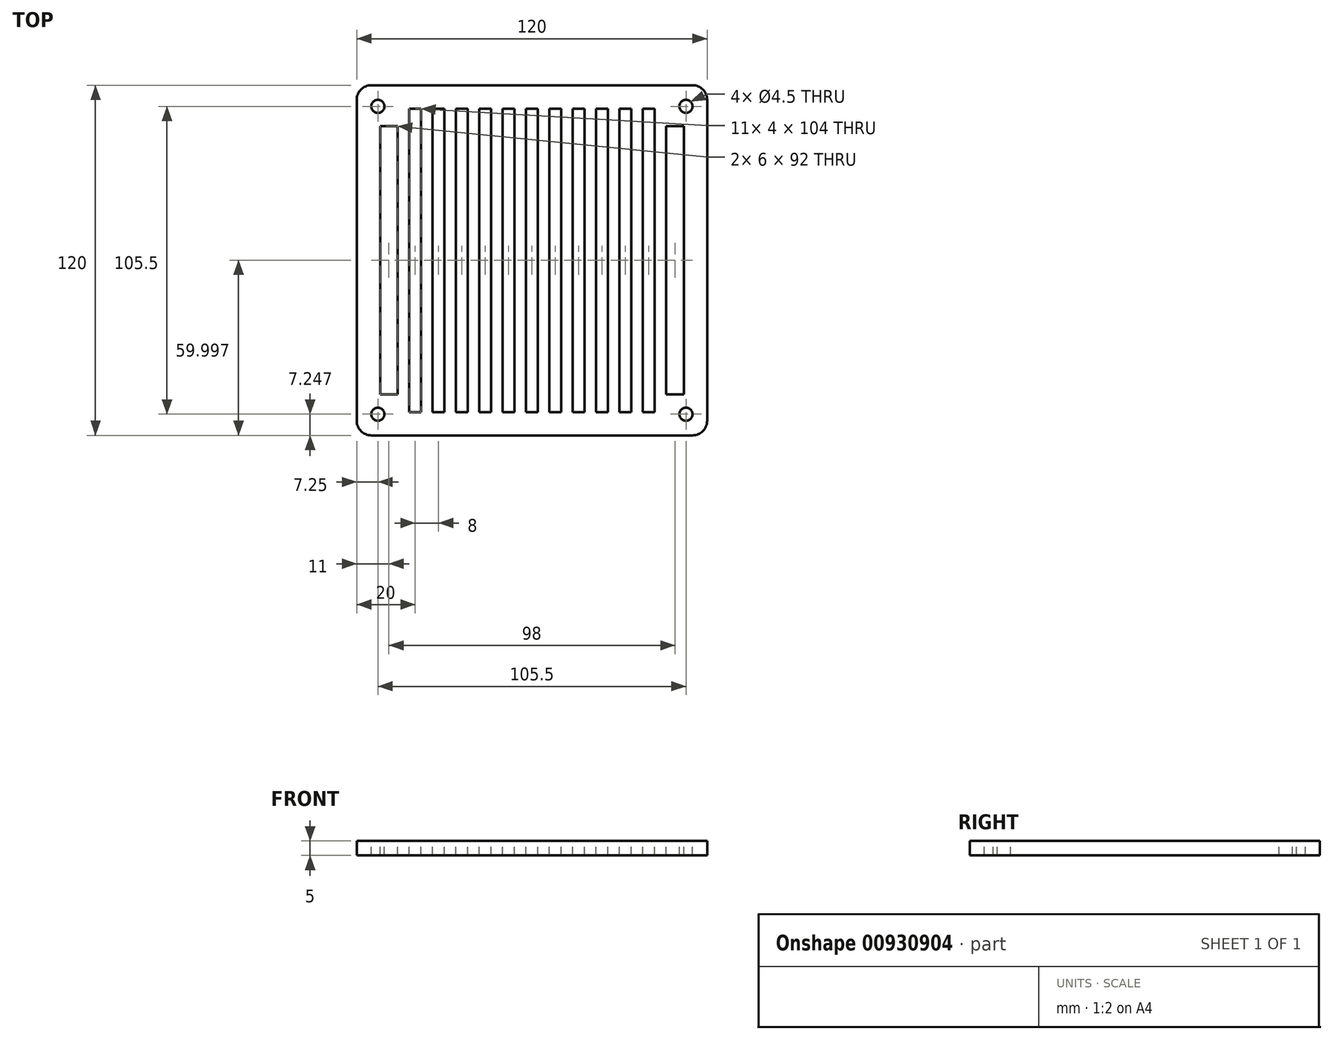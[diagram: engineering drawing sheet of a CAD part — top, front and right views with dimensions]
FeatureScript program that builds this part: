
annotation { "Feature Type Name" : "Feature", "Feature Type Description" : "" }
export const myFeature = defineFeature(function(context is Context, id is Id, definition is map)
    precondition{}
    {
        {
            var Q0;
            Q0=qCreatedBy(makeId("Top.planeOp"),FACE);
            var sketch = newSketch(context, id + "F0", { "sketchPlane" : qUnion([Q0])});
            skLineSegment(sketch, "E0", {"start": v(63.6, 60.5) * mm, "end": v(63.6, -59.5) * mm});
            skLineSegment(sketch, "E1", {"start": v(63.6, -59.5) * mm, "end": v(-56.4, -59.5) * mm});
            skLineSegment(sketch, "E2", {"start": v(63.6, 60.5) * mm, "end": v(-56.4, 60.5) * mm});
            skLineSegment(sketch, "E3", {"start": v(-56.4, 60.5) * mm, "end": v(-56.4, -59.5) * mm});
            skSolve(sketch);
        }
        {
            var Q0;
            Q0 = qSketchRegion(id + "F0", true);
            extrude(context, id + "F1", {"entities" : qUnion([Q0]), "depth" : 5 * mm, "offsetDistance" : 25 * mm});
        }
        {
            var Q0;
            Q0=makeQuery(id+"F1.opExtrude","SWEPT_EDGE",EDGE,{"disambiguationData":[OSD([sQuery(id+"F0.wireOp",EDGE,"E2"),sQuery(id+"F0.wireOp",EDGE,"E3")])]});
            var Q1;
            Q1=makeQuery(id+"F1.opExtrude","SWEPT_EDGE",EDGE,{"disambiguationData":[OSD([sQuery(id+"F0.wireOp",EDGE,"E0"),sQuery(id+"F0.wireOp",EDGE,"E2")])]});
            var Q2;
            Q2=makeQuery(id+"F1.opExtrude","SWEPT_EDGE",EDGE,{"disambiguationData":[OSD([sQuery(id+"F0.wireOp",EDGE,"E0"),sQuery(id+"F0.wireOp",EDGE,"E1")])]});
            var Q3;
            Q3=makeQuery(id+"F1.opExtrude","SWEPT_EDGE",EDGE,{"disambiguationData":[OSD([sQuery(id+"F0.wireOp",EDGE,"E1"),sQuery(id+"F0.wireOp",EDGE,"E3")])]});
            fillet(context, id + "F2", {"entities" : qUnion([Q0, Q1, Q2, Q3]), "radius" : 5 * mm, "tangentPropagation" : true, "allowEdgeOverflow" : false});
        }
        {
            var Q0;
            Q0=makeQuery(id+"F1.opExtrude","CAP_FACE",FACE,{"disambiguationData":[OSD([sQuery(id+"F0.wireOp",EDGE,"E0"),sQuery(id+"F0.wireOp",EDGE,"E1"),sQuery(id+"F0.wireOp",EDGE,"E2"),sQuery(id+"F0.wireOp",EDGE,"E3")])],"isStart":false});
            var sketch = newSketch(context, id + "F3", { "sketchPlane" : qUnion([Q0])});
            skCircle(sketch, "E4", {"center": v(-49.15, 53.25) * mm, "radius": 2.25 * mm});
            skLineSegment(sketch, "E5", {"start": v(63.6, 53.25) * mm, "end": v(30.25, 53.25) * mm});
            skLineSegment(sketch, "E6", {"start": v(56.35, 60.5) * mm, "end": v(56.35, 46.86) * mm});
            skCircle(sketch, "E7", {"center": v(56.35, 53.25) * mm, "radius": 2.25 * mm});
            skLineSegment(sketch, "E8", {"start": v(-49.15, -59.5) * mm, "end": v(-49.15, -31.18) * mm});
            skLineSegment(sketch, "E9", {"start": v(-56.4, -52.25) * mm, "end": v(-23.6, -52.25) * mm});
            skCircle(sketch, "E10", {"center": v(-49.15, -52.25) * mm, "radius": 2.25 * mm});
            skLineSegment(sketch, "E11", {"start": v(56.35, -59.5) * mm, "end": v(56.35, -31.04) * mm});
            skLineSegment(sketch, "E12", {"start": v(63.6, -52.25) * mm, "end": v(40.35, -52.25) * mm});
            skCircle(sketch, "E13", {"center": v(56.35, -52.25) * mm, "radius": 2.25 * mm});
            skSolve(sketch);
        }
        {
            var Q0;
            Q0 = qSketchRegion(id + "F3", true);
            extrude(context, id + "F4", {"entities" : qUnion([Q0]), "operationType" : NewBodyOperationType.REMOVE, "oppositeDirection" : true, "depth" : 25 * mm, "offsetDistance" : 25 * mm});
        }
        {
            var Q0;
            Q0=makeQuery(id+"F1.opExtrude","CAP_FACE",FACE,{"disambiguationData":[OSD([sQuery(id+"F0.wireOp",EDGE,"E0"),sQuery(id+"F0.wireOp",EDGE,"E1"),sQuery(id+"F0.wireOp",EDGE,"E2"),sQuery(id+"F0.wireOp",EDGE,"E3")])],"isStart":false});
            var sketch = newSketch(context, id + "F5", { "sketchPlane" : qUnion([Q0])});
            skLineSegment(sketch, "E14", {"start": v(-42.4, 60.5) * mm, "end": v(-42.4, -59.5) * mm});
            skLineSegment(sketch, "E15", {"start": v(49.6, 60.5) * mm, "end": v(49.6, -59.5) * mm});
            skLineSegment(sketch, "E16", {"start": v(-56.4, 46.5) * mm, "end": v(-38.4, 46.5) * mm});
            skLineSegment(sketch, "E17", {"start": v(-56.4, -45.5) * mm, "end": v(-38.4, -45.5) * mm});
            skLineSegment(sketch, "E18", {"start": v(-48.4, 46.5) * mm, "end": v(-48.4, -45.5) * mm});
            skLineSegment(sketch, "E19", {"start": v(55.6, 46.5) * mm, "end": v(55.6, -45.5) * mm});
            skLineSegment(sketch, "E20", {"start": v(-42.4, 52.5) * mm, "end": v(49.6, 52.5) * mm});
            skLineSegment(sketch, "E21", {"start": v(-42.4, -51.5) * mm, "end": v(49.6, -51.5) * mm});
            skLineSegment(sketch, "E22", {"start": v(-38.4, 52.5) * mm, "end": v(-38.4, -51.5) * mm});
            skLineSegment(sketch, "E23.1.0.0", {"start": v(-34.4, 52.5) * mm, "end": v(-34.4, -51.5) * mm});
            skLineSegment(sketch, "E23.2.0.0", {"start": v(-30.4, 52.5) * mm, "end": v(-30.4, -51.5) * mm});
            skLineSegment(sketch, "E23.3.0.0", {"start": v(-26.4, 52.5) * mm, "end": v(-26.4, -51.5) * mm});
            skLineSegment(sketch, "E23.4.0.0", {"start": v(-22.4, 52.5) * mm, "end": v(-22.4, -51.5) * mm});
            skLineSegment(sketch, "E23.5.0.0", {"start": v(-18.4, 52.5) * mm, "end": v(-18.4, -51.5) * mm});
            skLineSegment(sketch, "E23.6.0.0", {"start": v(-14.4, 52.5) * mm, "end": v(-14.4, -51.5) * mm});
            skLineSegment(sketch, "E23.7.0.0", {"start": v(-10.4, 52.5) * mm, "end": v(-10.4, -51.5) * mm});
            skLineSegment(sketch, "E23.8.0.0", {"start": v(-6.4, 52.5) * mm, "end": v(-6.4, -51.5) * mm});
            skLineSegment(sketch, "E23.9.0.0", {"start": v(-2.4, 52.5) * mm, "end": v(-2.4, -51.5) * mm});
            skLineSegment(sketch, "E23.10.0.0", {"start": v(1.6, 52.5) * mm, "end": v(1.6, -51.5) * mm});
            skLineSegment(sketch, "E23.11.0.0", {"start": v(5.6, 52.5) * mm, "end": v(5.6, -51.5) * mm});
            skLineSegment(sketch, "E23.12.0.0", {"start": v(9.6, 52.5) * mm, "end": v(9.6, -51.5) * mm});
            skLineSegment(sketch, "E23.13.0.0", {"start": v(13.6, 52.5) * mm, "end": v(13.6, -51.5) * mm});
            skLineSegment(sketch, "E23.14.0.0", {"start": v(17.6, 52.5) * mm, "end": v(17.6, -51.5) * mm});
            skLineSegment(sketch, "E23.15.0.0", {"start": v(21.6, 52.5) * mm, "end": v(21.6, -51.5) * mm});
            skLineSegment(sketch, "E23.16.0.0", {"start": v(25.6, 52.5) * mm, "end": v(25.6, -51.5) * mm});
            skLineSegment(sketch, "E23.17.0.0", {"start": v(29.6, 52.5) * mm, "end": v(29.6, -51.5) * mm});
            skLineSegment(sketch, "E23.18.0.0", {"start": v(33.6, 52.5) * mm, "end": v(33.6, -51.5) * mm});
            skLineSegment(sketch, "E23.19.0.0", {"start": v(37.6, 52.5) * mm, "end": v(37.6, -51.5) * mm});
            skLineSegment(sketch, "E23.20.0.0", {"start": v(41.6, 52.5) * mm, "end": v(41.6, -51.5) * mm});
            skLineSegment(sketch, "E23.21.0.0", {"start": v(45.6, 52.5) * mm, "end": v(45.6, -51.5) * mm});
            skLineSegment(sketch, "E23.direction1", {"start": v(-38.4, -51.5) * mm, "end": v(-34.4, -51.5) * mm, "construction": true});
            skLineSegment(sketch, "E24.trimOffspring", {"start": v(-34.4, -45.5) * mm, "end": v(-30.4, -45.5) * mm});
            skLineSegment(sketch, "E25.trimOffspring", {"start": v(-26.4, -45.5) * mm, "end": v(-22.4, -45.5) * mm});
            skLineSegment(sketch, "E26.trimOffspring", {"start": v(-18.4, -45.5) * mm, "end": v(-14.4, -45.5) * mm});
            skLineSegment(sketch, "E27.trimOffspring", {"start": v(-10.4, -45.5) * mm, "end": v(-6.4, -45.5) * mm});
            skLineSegment(sketch, "E28.trimOffspring", {"start": v(-2.4, -45.5) * mm, "end": v(1.6, -45.5) * mm});
            skLineSegment(sketch, "E29.trimOffspring", {"start": v(5.6, -45.5) * mm, "end": v(9.6, -45.5) * mm});
            skLineSegment(sketch, "E30.trimOffspring", {"start": v(13.6, -45.5) * mm, "end": v(17.6, -45.5) * mm});
            skLineSegment(sketch, "E31.trimOffspring", {"start": v(21.6, -45.5) * mm, "end": v(25.6, -45.5) * mm});
            skLineSegment(sketch, "E32.trimOffspring", {"start": v(29.6, -45.5) * mm, "end": v(33.6, -45.5) * mm});
            skLineSegment(sketch, "E33.trimOffspring", {"start": v(37.6, -45.5) * mm, "end": v(41.6, -45.5) * mm});
            skLineSegment(sketch, "E34.trimOffspring", {"start": v(45.6, -45.5) * mm, "end": v(63.6, -45.5) * mm});
            skLineSegment(sketch, "E35.trimOffspring", {"start": v(45.6, 46.5) * mm, "end": v(63.6, 46.5) * mm});
            skLineSegment(sketch, "E36.trimOffspring", {"start": v(37.6, 46.5) * mm, "end": v(41.6, 46.5) * mm});
            skLineSegment(sketch, "E37.trimOffspring", {"start": v(29.6, 46.5) * mm, "end": v(33.6, 46.5) * mm});
            skLineSegment(sketch, "E38.trimOffspring", {"start": v(21.6, 46.5) * mm, "end": v(25.6, 46.5) * mm});
            skLineSegment(sketch, "E39.trimOffspring", {"start": v(13.6, 46.5) * mm, "end": v(17.6, 46.5) * mm});
            skLineSegment(sketch, "E40.trimOffspring", {"start": v(5.6, 46.5) * mm, "end": v(9.6, 46.5) * mm});
            skLineSegment(sketch, "E41.trimOffspring", {"start": v(-2.4, 46.5) * mm, "end": v(1.6, 46.5) * mm});
            skLineSegment(sketch, "E42.trimOffspring", {"start": v(-10.4, 46.5) * mm, "end": v(-6.4, 46.5) * mm});
            skLineSegment(sketch, "E43.trimOffspring", {"start": v(-18.4, 46.5) * mm, "end": v(-14.4, 46.5) * mm});
            skLineSegment(sketch, "E44.trimOffspring", {"start": v(-26.4, 46.5) * mm, "end": v(-22.4, 46.5) * mm});
            skLineSegment(sketch, "E45.trimOffspring", {"start": v(-34.4, 46.5) * mm, "end": v(-30.4, 46.5) * mm});
            skSolve(sketch);
        }
        {
            var Q0;
            {var subQ5=sQuery(id+"F5.wireOp",EDGE,"E18");Q0=makeQuery(id+"F5.imprint","IMPRINT",FACE,{"disambiguationData":[TD([[makeQuery(id+"F5.imprint","IMPRINT",EDGE,{"derivedFrom":subQ5}),1.0]])]});}
            extrude(context, id + "F6", {"entities" : qUnion([Q0]), "operationType" : NewBodyOperationType.REMOVE, "oppositeDirection" : true, "depth" : 25 * mm, "offsetDistance" : 25 * mm});
        }
        {
            var Q0;
            {var subQ0=sQuery(id+"F5.wireOp",EDGE,"E22");var subQ7=sQuery(id+"F5.wireOp",EDGE,"E20");var subQ8=makeQuery(id+"F5.imprint","INTERSECT",VERTEX,{"derivedFrom":[subQ7,subQ0]});Q0=makeQuery(id+"F5.imprint","IMPRINT",FACE,{"disambiguationData":[TD([[makeQuery(id+"F5.imprint","IMPRINT",EDGE,{"disambiguationData":[TD([[subQ8,-1.0]])],"derivedFrom":subQ7}),-1.0]])]});}
            var Q1;
            {var subQ0=sQuery(id+"F5.wireOp",EDGE,"E23.2.0.0");var subQ1=sQuery(id+"F5.wireOp",EDGE,"E20");var subQ2=makeQuery(id+"F5.imprint","INTERSECT",VERTEX,{"derivedFrom":[subQ1,subQ0]});Q1=makeQuery(id+"F5.imprint","IMPRINT",FACE,{"disambiguationData":[TD([[makeQuery(id+"F5.imprint","IMPRINT",EDGE,{"disambiguationData":[TD([[subQ2,-1.0]])],"derivedFrom":subQ1}),-1.0]])]});}
            var Q2;
            {var subQ0=sQuery(id+"F5.wireOp",EDGE,"E23.4.0.0");var subQ3=sQuery(id+"F5.wireOp",EDGE,"E20");var subQ4=makeQuery(id+"F5.imprint","INTERSECT",VERTEX,{"derivedFrom":[subQ3,subQ0]});Q2=makeQuery(id+"F5.imprint","IMPRINT",FACE,{"disambiguationData":[TD([[makeQuery(id+"F5.imprint","IMPRINT",EDGE,{"disambiguationData":[TD([[subQ4,-1.0]])],"derivedFrom":subQ3}),-1.0]])]});}
            var Q3;
            {var subQ0=sQuery(id+"F5.wireOp",EDGE,"E23.6.0.0");var subQ1=sQuery(id+"F5.wireOp",EDGE,"E20");var subQ2=makeQuery(id+"F5.imprint","INTERSECT",VERTEX,{"derivedFrom":[subQ1,subQ0]});Q3=makeQuery(id+"F5.imprint","IMPRINT",FACE,{"disambiguationData":[TD([[makeQuery(id+"F5.imprint","IMPRINT",EDGE,{"disambiguationData":[TD([[subQ2,-1.0]])],"derivedFrom":subQ1}),-1.0]])]});}
            var Q4;
            {var subQ0=sQuery(id+"F5.wireOp",EDGE,"E23.8.0.0");var subQ3=sQuery(id+"F5.wireOp",EDGE,"E20");var subQ4=makeQuery(id+"F5.imprint","INTERSECT",VERTEX,{"derivedFrom":[subQ3,subQ0]});Q4=makeQuery(id+"F5.imprint","IMPRINT",FACE,{"disambiguationData":[TD([[makeQuery(id+"F5.imprint","IMPRINT",EDGE,{"disambiguationData":[TD([[subQ4,-1.0]])],"derivedFrom":subQ3}),-1.0]])]});}
            var Q5;
            {var subQ0=sQuery(id+"F5.wireOp",EDGE,"E23.10.0.0");var subQ3=sQuery(id+"F5.wireOp",EDGE,"E20");var subQ4=makeQuery(id+"F5.imprint","INTERSECT",VERTEX,{"derivedFrom":[subQ3,subQ0]});Q5=makeQuery(id+"F5.imprint","IMPRINT",FACE,{"disambiguationData":[TD([[makeQuery(id+"F5.imprint","IMPRINT",EDGE,{"disambiguationData":[TD([[subQ4,-1.0]])],"derivedFrom":subQ3}),-1.0]])]});}
            var Q6;
            {var subQ0=sQuery(id+"F5.wireOp",EDGE,"E23.12.0.0");var subQ1=sQuery(id+"F5.wireOp",EDGE,"E20");var subQ2=makeQuery(id+"F5.imprint","INTERSECT",VERTEX,{"derivedFrom":[subQ1,subQ0]});Q6=makeQuery(id+"F5.imprint","IMPRINT",FACE,{"disambiguationData":[TD([[makeQuery(id+"F5.imprint","IMPRINT",EDGE,{"disambiguationData":[TD([[subQ2,-1.0]])],"derivedFrom":subQ1}),-1.0]])]});}
            var Q7;
            {var subQ0=sQuery(id+"F5.wireOp",EDGE,"E23.14.0.0");var subQ3=sQuery(id+"F5.wireOp",EDGE,"E20");var subQ4=makeQuery(id+"F5.imprint","INTERSECT",VERTEX,{"derivedFrom":[subQ3,subQ0]});Q7=makeQuery(id+"F5.imprint","IMPRINT",FACE,{"disambiguationData":[TD([[makeQuery(id+"F5.imprint","IMPRINT",EDGE,{"disambiguationData":[TD([[subQ4,-1.0]])],"derivedFrom":subQ3}),-1.0]])]});}
            var Q8;
            {var subQ0=sQuery(id+"F5.wireOp",EDGE,"E23.16.0.0");var subQ1=sQuery(id+"F5.wireOp",EDGE,"E20");var subQ2=makeQuery(id+"F5.imprint","INTERSECT",VERTEX,{"derivedFrom":[subQ1,subQ0]});Q8=makeQuery(id+"F5.imprint","IMPRINT",FACE,{"disambiguationData":[TD([[makeQuery(id+"F5.imprint","IMPRINT",EDGE,{"disambiguationData":[TD([[subQ2,-1.0]])],"derivedFrom":subQ1}),-1.0]])]});}
            var Q9;
            {var subQ0=sQuery(id+"F5.wireOp",EDGE,"E23.18.0.0");var subQ3=sQuery(id+"F5.wireOp",EDGE,"E20");var subQ4=makeQuery(id+"F5.imprint","INTERSECT",VERTEX,{"derivedFrom":[subQ3,subQ0]});Q9=makeQuery(id+"F5.imprint","IMPRINT",FACE,{"disambiguationData":[TD([[makeQuery(id+"F5.imprint","IMPRINT",EDGE,{"disambiguationData":[TD([[subQ4,-1.0]])],"derivedFrom":subQ3}),-1.0]])]});}
            var Q10;
            {var subQ0=sQuery(id+"F5.wireOp",EDGE,"E23.20.0.0");var subQ9=sQuery(id+"F5.wireOp",EDGE,"E20");var subQ10=makeQuery(id+"F5.imprint","INTERSECT",VERTEX,{"derivedFrom":[subQ9,subQ0]});Q10=makeQuery(id+"F5.imprint","IMPRINT",FACE,{"disambiguationData":[TD([[makeQuery(id+"F5.imprint","IMPRINT",EDGE,{"disambiguationData":[TD([[subQ10,-1.0]])],"derivedFrom":subQ9}),-1.0]])]});}
            extrude(context, id + "F7", {"entities" : qUnion([Q0, Q1, Q2, Q3, Q4, Q5, Q6, Q7, Q8, Q9, Q10]), "operationType" : NewBodyOperationType.REMOVE, "oppositeDirection" : true, "depth" : 25 * mm, "offsetDistance" : 25 * mm});
        }
        {
            var Q0;
            {var subQ5=sQuery(id+"F5.wireOp",EDGE,"E19");Q0=makeQuery(id+"F5.imprint","IMPRINT",FACE,{"disambiguationData":[TD([[makeQuery(id+"F5.imprint","IMPRINT",EDGE,{"derivedFrom":subQ5}),-1.0]])]});}
            extrude(context, id + "F8", {"entities" : qUnion([Q0]), "operationType" : NewBodyOperationType.REMOVE, "oppositeDirection" : true, "depth" : 25 * mm, "offsetDistance" : 25 * mm});
        }
    });
